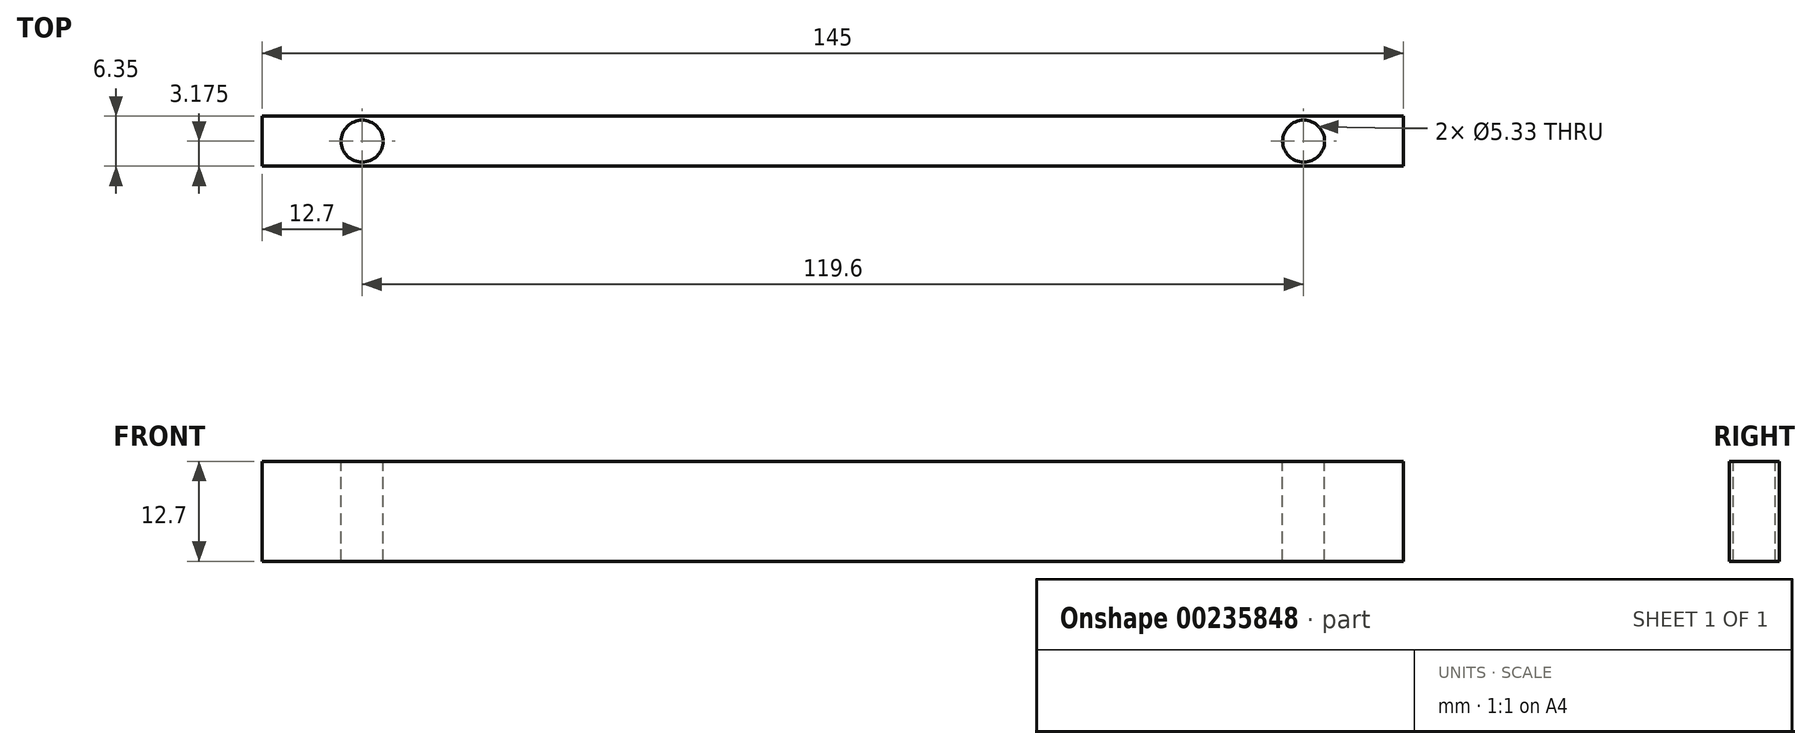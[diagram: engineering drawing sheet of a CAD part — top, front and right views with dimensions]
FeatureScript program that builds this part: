
annotation { "Feature Type Name" : "Feature", "Feature Type Description" : "" }
export const myFeature = defineFeature(function(context is Context, id is Id, definition is map)
    precondition{}
    {
        {
            var Q0;
            Q0=qCreatedBy(makeId("Front.planeOp"),FACE);
            var sketch = newSketch(context, id + "F0", { "sketchPlane" : qUnion([Q0])});
            skLineSegment(sketch, "E0.bottom", {"start": v(0, 0) * mm, "end": v(145, 0) * mm});
            skLineSegment(sketch, "E0.top", {"start": v(0, 12.7) * mm, "end": v(145, 12.7) * mm});
            skLineSegment(sketch, "E0.left", {"start": v(0, 0) * mm, "end": v(0, 12.7) * mm});
            skLineSegment(sketch, "E0.right", {"start": v(145, 0) * mm, "end": v(145, 12.7) * mm});
            skSolve(sketch);
        }
        {
            var Q0;
            Q0=makeQuery(id+"F0.imprint","IMPRINT",FACE,{"disambiguationData":[TD([[makeQuery(id+"F0.imprint","IMPRINT",EDGE,{"derivedFrom":sQuery(id+"F0.wireOp",EDGE,"E0.bottom")}),1.0]])]});
            extrude(context, id + "F1", {"entities" : qUnion([Q0]), "depth" : 6.35 * mm});
        }
        {
            var Q0;
            Q0=makeQuery(id+"F1.opExtrude","SWEPT_FACE",FACE,{"disambiguationData":[OSD([sQuery(id+"F0.wireOp",EDGE,"E0.top")])]});
            var sketch = newSketch(context, id + "F2", { "sketchPlane" : qUnion([Q0])});
            skPoint(sketch, "E1", {"position": v(12.7, -3.18) * mm});
            skPoint(sketch, "E2", {"position": v(173.06, -3.17) * mm});
            skPoint(sketch, "E3", {"position": v(132.3, -3.17) * mm});
            skSolve(sketch);
        }
        {
            var Q0;
            Q0=sQuery(id+"F2.wireOp",VERTEX,"E1");
            var Q1;
            Q1=sQuery(id+"F2.wireOp",VERTEX,"E3");
            var Q2;
            Q2=makeQuery(id+"F1.opExtrude","SWEPT_BODY",BODY,{"disambiguationData":[OSD([sQuery(id+"F0.wireOp",EDGE,"E0.bottom"),sQuery(id+"F0.wireOp",EDGE,"E0.top"),sQuery(id+"F0.wireOp",EDGE,"E0.left"),sQuery(id+"F0.wireOp",EDGE,"E0.right")])]});
            hole(context, id + "F3", {"style" : HoleStyle.SIMPLE, "endStyle" : HoleEndStyle.BLIND, "holeDiameter" : 5.33 * mm, "holeDepth" : 12.7 * mm, "locations" : qUnion([Q0, Q1]), "scope" : qUnion([Q2])});
        }
    });
